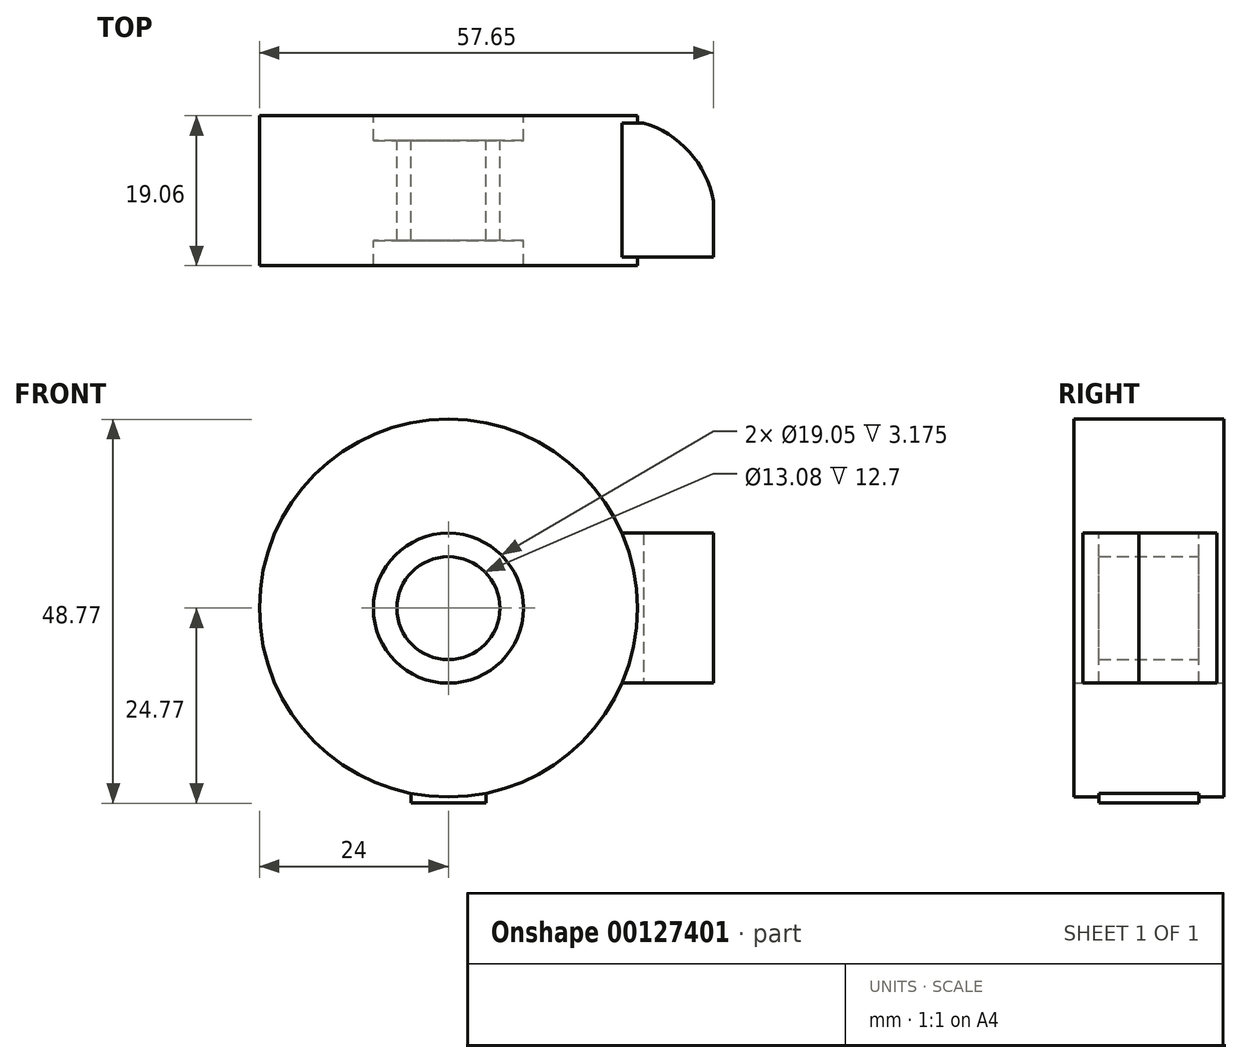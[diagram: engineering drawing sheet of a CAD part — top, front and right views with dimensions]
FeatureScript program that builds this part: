
annotation { "Feature Type Name" : "Feature", "Feature Type Description" : "" }
export const myFeature = defineFeature(function(context is Context, id is Id, definition is map)
    precondition{}
    {
        {
            var Q0;
            Q0=qCreatedBy(makeId("Front.planeOp"),FACE);
            var sketch = newSketch(context, id + "F0", { "sketchPlane" : qUnion([Q0])});
            skCircle(sketch, "E0", {"center": v(0, 0) * mm, "radius": 24 * mm});
            skCircle(sketch, "E1", {"center": v(0, 0) * mm, "radius": 9.53 * mm});
            skSolve(sketch);
        }
        {
            var Q0;
            Q0 = qSketchRegion(id + "F0", true);
            extrude(context, id + "F1", {"entities" : qUnion([Q0]), "endBound" : BoundingType.SYMMETRIC, "depth" : 19.05 * mm});
        }
        {
            var Q0;
            Q0=qCreatedBy(makeId("Front.planeOp"),FACE);
            var sketch = newSketch(context, id + "F2", { "sketchPlane" : qUnion([Q0])});
            skCircle(sketch, "E2", {"center": v(0, 0) * mm, "radius": 6.54 * mm});
            skArc(sketch, "E3", {"start": v(4.76, -17.79) * mm, "mid": v(0, 18.41) * mm, "end": v(-4.76, -17.79) * mm});
            skLineSegment(sketch, "E4.top", {"start": v(4.76, -24.77) * mm, "end": v(-4.76, -24.77) * mm});
            skLineSegment(sketch, "E4.left", {"start": v(4.76, -17.79) * mm, "end": v(4.76, -24.77) * mm});
            skLineSegment(sketch, "E4.right", {"start": v(-4.76, -17.79) * mm, "end": v(-4.76, -24.77) * mm});
            skPoint(sketch, "E4.middle", {"position": v(0, -20.6) * mm});
            skPoint(sketch, "E4.bottom.end.orphan", {"position": v(-4.76, -16.42) * mm});
            skPoint(sketch, "E4.bottom.start.orphan", {"position": v(4.76, -16.42) * mm});
            skSolve(sketch);
        }
        {
            var Q0;
            Q0 = qSketchRegion(id + "F2", true);
            extrude(context, id + "F3", {"entities" : qUnion([Q0]), "endBound" : BoundingType.SYMMETRIC, "depth" : 12.7 * mm});
        }
        {
            var Q0;
            Q0=qCreatedBy(makeId("Top.planeOp"),FACE);
            var sketch = newSketch(context, id + "F4", { "sketchPlane" : qUnion([Q0])});
            skLineSegment(sketch, "E5.bottom", {"start": v(9.53, -8.4) * mm, "end": v(24, -8.4) * mm});
            skLineSegment(sketch, "E5.top", {"start": v(15.88, 8.63) * mm, "end": v(17.65, 8.63) * mm});
            skLineSegment(sketch, "E5.left", {"start": v(9.53, -8.4) * mm, "end": v(9.53, 2.28) * mm});
            skLineSegment(sketch, "E5.right", {"start": v(24, -8.4) * mm, "end": v(24, 2.28) * mm});
            skLineSegment(sketch, "E6", {"start": v(0, 35.12) * mm, "end": v(0, -36.52) * mm, "construction": true});
            skPoint(sketch, "E7.visualSharp", {"position": v(24, 8.63) * mm});
            skArc(sketch, "E7.filletArc", {"start": v(24, 2.28) * mm, "mid": v(22.14, 6.77) * mm, "end": v(17.65, 8.63) * mm});
            skPoint(sketch, "E8.visualSharp", {"position": v(9.53, 8.63) * mm});
            skArc(sketch, "E8.filletArc", {"start": v(15.88, 8.63) * mm, "mid": v(11.38, 6.77) * mm, "end": v(9.53, 2.28) * mm});
            skSolve(sketch);
        }
        {
            var Q0;
            Q0 = qSketchRegion(id + "F4", true);
            var Q1;
            Q1=sQuery(id+"F4.wireOp",EDGE,"E6");
            revolve(context, id + "F5", {"entities" : qUnion([Q0]), "axis" : qUnion([Q1]), "revolveType" : RevolveType.FULL});
        }
        {
            var Q0;
            Q0=qCreatedBy(makeId("Top.planeOp"),FACE);
            var sketch = newSketch(context, id + "F6", { "sketchPlane" : qUnion([Q0])});
            skLineSegment(sketch, "E9.bottom", {"start": v(17.65, 8.63) * mm, "end": v(24.76, 8.63) * mm});
            skLineSegment(sketch, "E9.top", {"start": v(17.65, -8.4) * mm, "end": v(33.66, -8.4) * mm});
            skLineSegment(sketch, "E9.left", {"start": v(17.65, 8.63) * mm, "end": v(17.65, -8.4) * mm});
            skLineSegment(sketch, "E9.right", {"start": v(33.66, -1.28) * mm, "end": v(33.66, -8.4) * mm});
            skArc(sketch, "E10", {"start": v(33.66, -1.28) * mm, "mid": v(30.61, 4.93) * mm, "end": v(24.76, 8.63) * mm});
            skSolve(sketch);
        }
        {
            var Q0;
            Q0 = qSketchRegion(id + "F6", true);
            extrude(context, id + "F7", {"entities" : qUnion([Q0]), "operationType" : NewBodyOperationType.ADD, "endBound" : BoundingType.SYMMETRIC, "depth" : 19.05 * mm});
        }
    });
